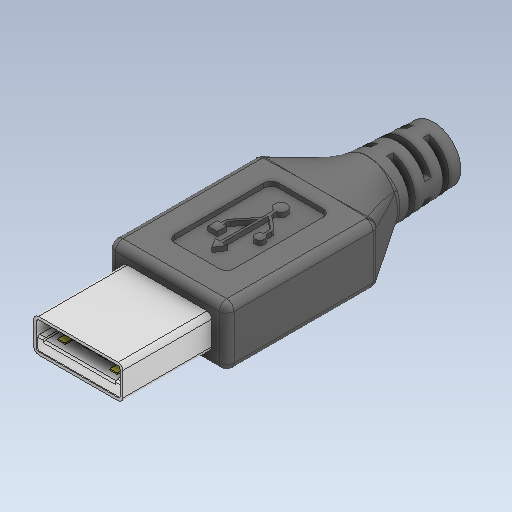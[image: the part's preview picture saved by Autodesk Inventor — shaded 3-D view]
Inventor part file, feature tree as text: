
AUTODESK INVENTOR PART (.ipt)
format: ipt  version: 2021 (Build 250183000, 183)  size: 505,344 bytes
history: native  units: in
note: dims shown in document units (in); Inventor stores cm internally (conversion verified against a paired STEP export)
features: fillet x1
ambient origin geometry x8: Origin, YZ Plane, XZ Plane, XY Plane, X Axis, Y Axis, Z Axis, Center Point
bodies: Solid1 (feature_tree)
feature tree (1):
  fillet  "Fillet6"  [1 undecoded]
note: 1 required parameter value undecoded (feature->parameter linkage not recoverable at this tier; creation-order binding heuristic only, values carry confidence <= 0.55)
